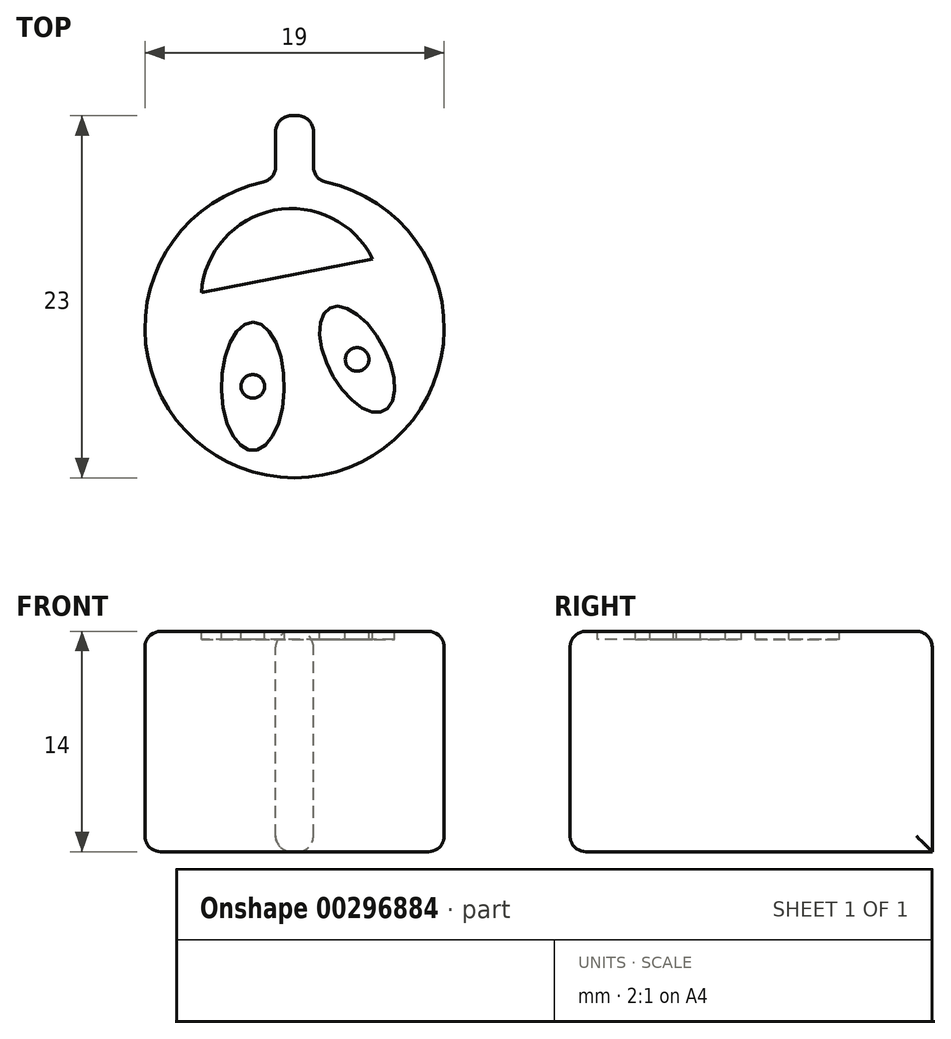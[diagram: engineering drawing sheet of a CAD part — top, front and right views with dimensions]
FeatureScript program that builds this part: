
annotation { "Feature Type Name" : "Feature", "Feature Type Description" : "" }
export const myFeature = defineFeature(function(context is Context, id is Id, definition is map)
    precondition{}
    {
        {
            var Q0;
            Q0=qCreatedBy(makeId("Top.planeOp"),FACE);
            var sketch = newSketch(context, id + "F0", { "sketchPlane" : qUnion([Q0])});
            skCircle(sketch, "E0", {"center": v(0, 0) * mm, "radius": 9.5 * mm});
            skSolve(sketch);
        }
        {
            var Q0;
            Q0 = qSketchRegion(id + "F0", true);
            extrude(context, id + "F1", {"entities" : qUnion([Q0]), "depth" : 12 * mm});
        }
        {
            var Q0;
            Q0=qCreatedBy(makeId("Front.planeOp"),FACE);
            var sketch = newSketch(context, id + "F2", { "sketchPlane" : qUnion([Q0])});
            skLineSegment(sketch, "E1", {"start": v(-2, 0) * mm, "end": v(-1.76, -7) * mm});
            skLineSegment(sketch, "E2", {"start": v(-1.76, -7) * mm, "end": v(-3.66, -7) * mm});
            skLineSegment(sketch, "E3", {"start": v(-3.66, -7) * mm, "end": v(-4.02, 0) * mm});
            skLineSegment(sketch, "E4", {"start": v(-4.02, 0) * mm, "end": v(-2, 0) * mm});
            skSolve(sketch);
        }
        {
            var Q0;
            Q0=makeQuery(id+"F1.opExtrude","CAP_FACE",FACE,{"disambiguationData":[OSD([sQuery(id+"F0.wireOp",EDGE,"E0")])],"isStart":false});
            var sketch = newSketch(context, id + "F3", { "sketchPlane" : qUnion([Q0])});
            skLineSegment(sketch, "E5.bottom", {"start": v(1.2, 13.5) * mm, "end": v(-1.2, 13.5) * mm});
            skLineSegment(sketch, "E5.top", {"start": v(1.2, 0) * mm, "end": v(-1.2, 0) * mm});
            skLineSegment(sketch, "E5.left", {"start": v(1.2, 13.5) * mm, "end": v(1.2, 0) * mm});
            skLineSegment(sketch, "E5.right", {"start": v(-1.2, 13.5) * mm, "end": v(-1.2, 0) * mm});
            skPoint(sketch, "E5.middle", {"position": v(0, 6.75) * mm});
            skSolve(sketch);
        }
        {
            var Q0;
            Q0 = qSketchRegion(id + "F3", true);
            var Q1;
            Q1=makeQuery(id+"F1.opExtrude","CAP_FACE",FACE,{"disambiguationData":[OSD([sQuery(id+"F0.wireOp",EDGE,"E0")])],"isStart":true});
            extrude(context, id + "F4", {"entities" : qUnion([Q0]), "operationType" : NewBodyOperationType.ADD, "endBound" : BoundingType.UP_TO_SURFACE, "oppositeDirection" : true, "endBoundEntityFace" : qUnion([Q1]), "depth" : 25 * mm});
        }
        {
            var Q0;
            Q0=makeQuery(id+"F4.boolean.opBoolean","MERGE",FACE,{"derivedFrom":[makeQuery(id+"F1.opExtrude","CAP_FACE",FACE,{"disambiguationData":[OSD([sQuery(id+"F0.wireOp",EDGE,"E0")])],"isStart":false}),makeQuery(id+"F4.opExtrude","CAP_FACE",FACE,{"disambiguationData":[OSD([sQuery(id+"F3.wireOp",EDGE,"E5.bottom"),sQuery(id+"F3.wireOp",EDGE,"E5.top"),sQuery(id+"F3.wireOp",EDGE,"E5.left"),sQuery(id+"F3.wireOp",EDGE,"E5.right")])],"isStart":true})]});
            cPlane(context, id + "F5", {"entities" : qUnion([Q0]), "cplaneType" : CPlaneType.OFFSET, "offset" : 6 * mm, "oppositeDirection" : true, "width" : 150 * mm, "height" : 150 * mm});
        }
        {
            var Q0;
            Q0=qCreatedBy(id+"F5.planeOp",FACE);
            var sketch = newSketch(context, id + "F6", { "sketchPlane" : qUnion([Q0])});
            skLineSegment(sketch, "E6", {"start": v(0, 0) * mm, "end": v(-3.8, 15.79) * mm});
            skLineSegment(sketch, "E7", {"start": v(-13.84, 8.48) * mm, "end": v(0, 0) * mm});
            skLineSegment(sketch, "E8", {"start": v(-13.84, 8.48) * mm, "end": v(-3.8, 15.79) * mm});
            skSolve(sketch);
        }
        {
            var Q0;
            Q0=makeQuery(id+"F4.boolean.opBoolean","MERGE",FACE,{"derivedFrom":[makeQuery(id+"F1.opExtrude","CAP_FACE",FACE,{"disambiguationData":[OSD([sQuery(id+"F0.wireOp",EDGE,"E0")])],"isStart":false}),makeQuery(id+"F4.opExtrude","CAP_FACE",FACE,{"disambiguationData":[OSD([sQuery(id+"F3.wireOp",EDGE,"E5.bottom"),sQuery(id+"F3.wireOp",EDGE,"E5.top"),sQuery(id+"F3.wireOp",EDGE,"E5.left"),sQuery(id+"F3.wireOp",EDGE,"E5.right")])],"isStart":true})]});
            var sketch = newSketch(context, id + "F7", { "sketchPlane" : qUnion([Q0])});
            skEllipse(sketch, "E9", {"center": v(-2.65, -3.7) * mm, "majorRadius": 4.07 * mm, "minorRadius": 2 * mm, "majorAxis": v(0, 1)});
            skEllipse(sketch, "E10", {"center": v(3.97, -1.98) * mm, "majorRadius": 3.7 * mm, "minorRadius": 1.85 * mm, "majorAxis": v(-0.47, 0.88)});
            skArc(sketch, "E11", {"start": v(4.96, 4.41) * mm, "mid": v(-1.29, 7.5) * mm, "end": v(-5.92, 2.28) * mm});
            skLineSegment(sketch, "E12", {"start": v(4.96, 4.41) * mm, "end": v(-5.92, 2.28) * mm});
            skCircle(sketch, "E13", {"center": v(3.97, -1.98) * mm, "radius": 0.75 * mm});
            skCircle(sketch, "E14", {"center": v(-2.65, -3.7) * mm, "radius": 0.75 * mm});
            skSolve(sketch);
        }
        {
            var Q0;
            Q0=makeQuery(id+"F7.imprint","IMPRINT",FACE,{"disambiguationData":[TD([[makeQuery(id+"F7.imprint","IMPRINT",EDGE,{"derivedFrom":sQuery(id+"F7.wireOp",EDGE,"E9")}),-1.0]])]});
            var Q1;
            Q1=makeQuery(id+"F7.imprint","IMPRINT",FACE,{"disambiguationData":[TD([[makeQuery(id+"F7.imprint","IMPRINT",EDGE,{"derivedFrom":sQuery(id+"F7.wireOp",EDGE,"E11")}),1.0]])]});
            var Q2;
            Q2=makeQuery(id+"F7.imprint","IMPRINT",FACE,{"disambiguationData":[TD([[makeQuery(id+"F7.imprint","IMPRINT",EDGE,{"derivedFrom":sQuery(id+"F7.wireOp",EDGE,"E9")}),1.0]])]});
            var Q3;
            Q3=makeQuery(id+"F7.imprint","IMPRINT",FACE,{"disambiguationData":[TD([[makeQuery(id+"F7.imprint","IMPRINT",EDGE,{"derivedFrom":sQuery(id+"F7.wireOp",EDGE,"E10")}),1.0]])]});
            var Q4;
            Q4=makeQuery(id+"F7.imprint","IMPRINT",FACE,{"disambiguationData":[TD([[makeQuery(id+"F7.imprint","IMPRINT",EDGE,{"derivedFrom":sQuery(id+"F7.wireOp",EDGE,"E14")}),1.0]])]});
            var Q5;
            Q5=makeQuery(id+"F7.imprint","IMPRINT",FACE,{"disambiguationData":[TD([[makeQuery(id+"F7.imprint","IMPRINT",EDGE,{"derivedFrom":sQuery(id+"F7.wireOp",EDGE,"E13")}),1.0]])]});
            extrude(context, id + "F8", {"entities" : qUnion([Q0, Q1, Q2, Q3, Q4, Q5]), "operationType" : NewBodyOperationType.ADD, "depth" : 2 * mm});
        }
        {
            var Q0;
            Q0=makeQuery(id+"F8.opExtrude","CAP_FACE",FACE,{"disambiguationData":[OSD([sQuery(id+"F0.wireOp",EDGE,"E0"),sQuery(id+"F3.wireOp",EDGE,"E5.bottom"),sQuery(id+"F3.wireOp",EDGE,"E5.left"),sQuery(id+"F3.wireOp",EDGE,"E5.right")])],"isStart":false});
            var sketch = newSketch(context, id + "F9", { "sketchPlane" : qUnion([Q0])});
            skPoint(sketch, "E15.0.end.orphan", {"position": v(-5.92, 2.28) * mm});
            skPoint(sketch, "E15.0.start.orphan", {"position": v(4.96, 4.41) * mm});
            skLineSegment(sketch, "E16.0.0", {"start": v(-5.92, 2.28) * mm, "end": v(4.96, 4.41) * mm});
            skArc(sketch, "E16.0.1", {"start": v(4.96, 4.41) * mm, "mid": v(-1.29, 7.5) * mm, "end": v(-5.92, 2.28) * mm});
            skEllipse(sketch, "E17.0.0", {"center": v(-2.65, -3.7) * mm, "majorRadius": 4.07 * mm, "minorRadius": 2 * mm, "majorAxis": v(0, 1)});
            skEllipse(sketch, "E18.0.0", {"center": v(3.97, -1.98) * mm, "majorRadius": 3.7 * mm, "minorRadius": 1.85 * mm, "majorAxis": v(-0.47, 0.88)});
            skCircle(sketch, "E19.0", {"center": v(-2.65, -3.7) * mm, "radius": 0.75 * mm});
            skCircle(sketch, "E20.0.0", {"center": v(3.97, -1.98) * mm, "radius": 0.75 * mm});
            skSolve(sketch);
        }
        {
            var Q0;
            Q0=makeQuery(id+"F9.imprint","IMPRINT",FACE,{"disambiguationData":[TD([[makeQuery(id+"F9.imprint","IMPRINT",EDGE,{"derivedFrom":sQuery(id+"F9.wireOp",EDGE,"E16.0.0")}),1.0]])]});
            var Q1;
            Q1=makeQuery(id+"F9.imprint","IMPRINT",FACE,{"disambiguationData":[TD([[makeQuery(id+"F9.imprint","IMPRINT",EDGE,{"derivedFrom":sQuery(id+"F9.wireOp",EDGE,"E17.0.0")}),1.0]])]});
            var Q2;
            Q2=makeQuery(id+"F9.imprint","IMPRINT",FACE,{"disambiguationData":[TD([[makeQuery(id+"F9.imprint","IMPRINT",EDGE,{"derivedFrom":sQuery(id+"F9.wireOp",EDGE,"E18.0.0")}),1.0]])]});
            extrude(context, id + "F10", {"entities" : qUnion([Q0, Q1, Q2]), "operationType" : NewBodyOperationType.REMOVE, "oppositeDirection" : true, "depth" : .5 * mm});
        }
        {
            var Q0;
            Q0=makeQuery(id+"F8.opExtrude","CAP_EDGE",EDGE,{"disambiguationData":[OSD([sQuery(id+"F0.wireOp",EDGE,"E0")])],"isStart":false});
            var Q1;
            Q1=makeQuery(id+"F8.opExtrude","CAP_EDGE",EDGE,{"disambiguationData":[OSD([sQuery(id+"F3.wireOp",EDGE,"E5.bottom")])],"isStart":false});
            var Q2;
            Q2=makeQuery(id+"F4.opExtrude","TWEAK_EDGE",EDGE,{"derivedFrom":[makeQuery(id+"F1.opExtrude","CAP_FACE",FACE,{"disambiguationData":[OSD([sQuery(id+"F0.wireOp",EDGE,"E0")])],"isStart":true}),makeQuery(id+"F3.imprint","IMPRINT",EDGE,{"derivedFrom":sQuery(id+"F3.wireOp",EDGE,"E5.bottom")})]});
            var Q3;
            Q3=makeQuery(id+"F1.opExtrude","CAP_EDGE",EDGE,{"disambiguationData":[OSD([sQuery(id+"F0.wireOp",EDGE,"E0")])],"isStart":true});
            fillet(context, id + "F11", {"entities" : qUnion([Q0, Q1, Q2, Q3]), "radius" : 1 * mm, "tangentPropagation" : true, "allowEdgeOverflow" : false});
        }
        {
            var Q0;
            {var subQ0=sQuery(id+"F3.wireOp",EDGE,"E5.left");Q0=makeQuery(id+"F8.boolean.opBoolean","MERGE",FACE,{"derivedFrom":[makeQuery(id+"F4.opExtrude","SWEPT_FACE",FACE,{"disambiguationData":[OSD([subQ0])]}),makeQuery(id+"F8.opExtrude","SWEPT_FACE",FACE,{"disambiguationData":[OSD([subQ0])]})]});}
            var Q1;
            {var subQ0=sQuery(id+"F3.wireOp",EDGE,"E5.right");Q1=makeQuery(id+"F8.boolean.opBoolean","MERGE",FACE,{"derivedFrom":[makeQuery(id+"F4.opExtrude","SWEPT_FACE",FACE,{"disambiguationData":[OSD([subQ0])]}),makeQuery(id+"F8.opExtrude","SWEPT_FACE",FACE,{"disambiguationData":[OSD([subQ0])]})]});}
            fillet(context, id + "F12", {"entities" : qUnion([Q0, Q1]), "radius" : 1 * mm, "tangentPropagation" : true, "allowEdgeOverflow" : false});
        }
    });
